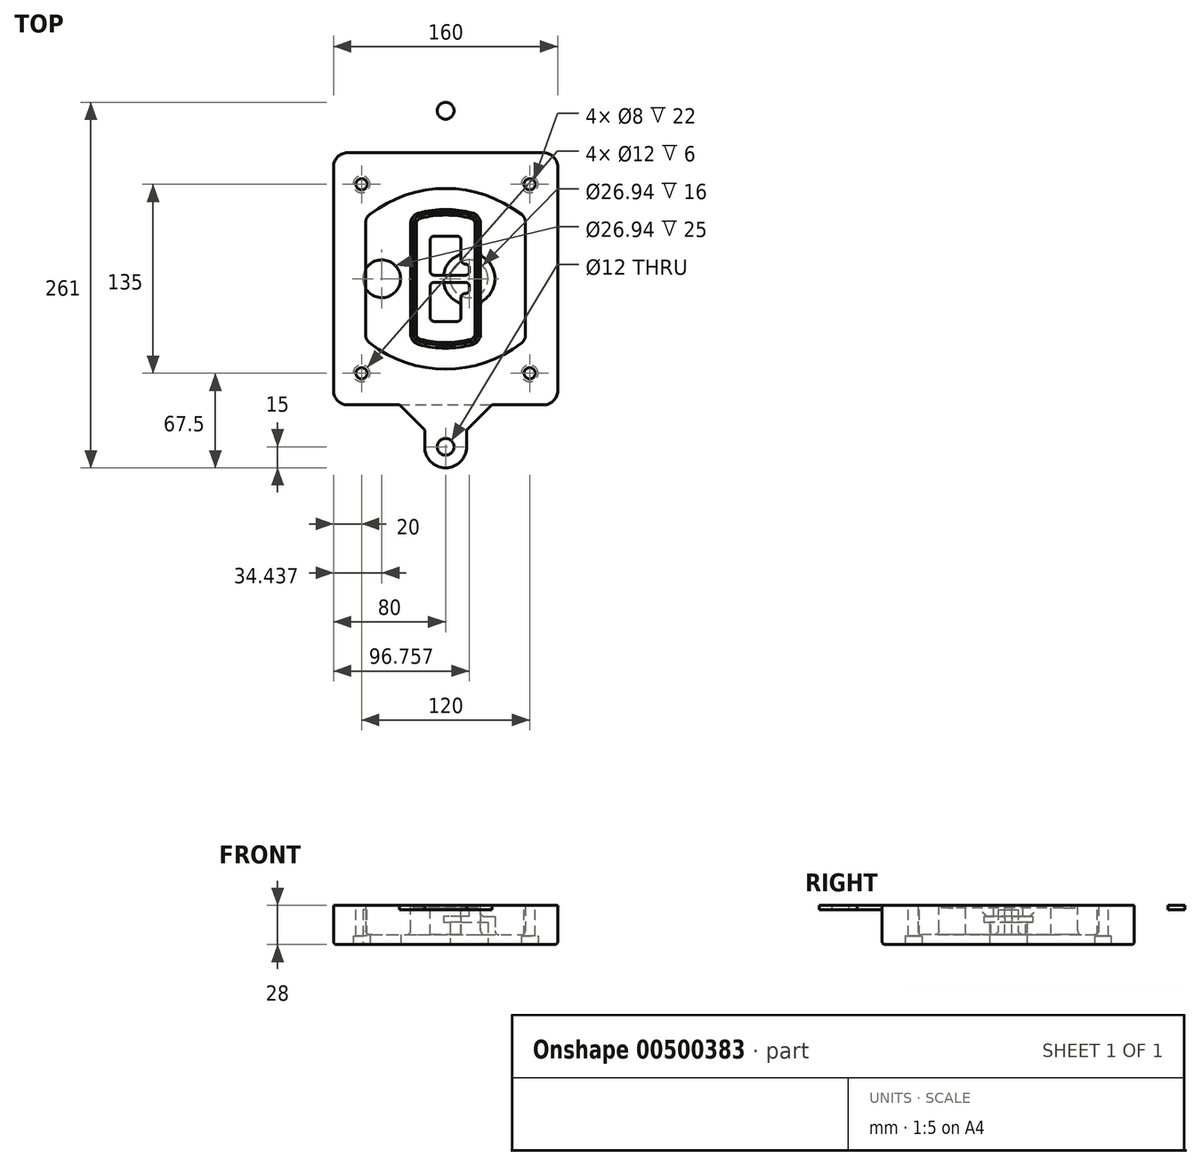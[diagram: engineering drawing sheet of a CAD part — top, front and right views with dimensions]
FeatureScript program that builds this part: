
annotation { "Feature Type Name" : "Feature", "Feature Type Description" : "" }
export const myFeature = defineFeature(function(context is Context, id is Id, definition is map)
    precondition{}
    {
        {
            var Q0;
            Q0=qCreatedBy(makeId("Top.planeOp"),FACE);
            var sketch = newSketch(context, id + "F0", { "sketchPlane" : qUnion([Q0])});
            skPoint(sketch, "E0.rect.middle", {"position": v(0, 0) * mm});
            skLineSegment(sketch, "E1.bottom", {"start": v(-70, -90) * mm, "end": v(70, -90) * mm});
            skLineSegment(sketch, "E1.top", {"start": v(-70, 90) * mm, "end": v(70, 90) * mm});
            skLineSegment(sketch, "E1.left", {"start": v(-80, -80) * mm, "end": v(-80, 80) * mm});
            skLineSegment(sketch, "E1.right", {"start": v(80, -80) * mm, "end": v(80, 80) * mm});
            skLineSegment(sketch, "E2", {"start": v(-80, 90) * mm, "end": v(80, -90) * mm, "construction": true});
            skLineSegment(sketch, "E3", {"start": v(80, 90) * mm, "end": v(-80, -90) * mm, "construction": true});
            skCircle(sketch, "E4", {"center": v(-60, 67.5) * mm, "radius": 4 * mm});
            skCircle(sketch, "E5", {"center": v(60, 67.5) * mm, "radius": 4 * mm});
            skCircle(sketch, "E6", {"center": v(60, -67.5) * mm, "radius": 4 * mm});
            skCircle(sketch, "E7", {"center": v(-60, -67.5) * mm, "radius": 4 * mm});
            skLineSegment(sketch, "E8", {"start": v(-60, 67.5) * mm, "end": v(60, 67.5) * mm, "construction": true});
            skLineSegment(sketch, "E9", {"start": v(60, 67.5) * mm, "end": v(60, -67.5) * mm, "construction": true});
            skLineSegment(sketch, "E10", {"start": v(60, -67.5) * mm, "end": v(-60, -67.5) * mm, "construction": true});
            skLineSegment(sketch, "E11", {"start": v(-60, -67.5) * mm, "end": v(-60, 67.5) * mm, "construction": true});
            skLineSegment(sketch, "E12", {"start": v(-60, 40.3) * mm, "end": v(-60, -40.3) * mm});
            skLineSegment(sketch, "E13", {"start": v(60, 40.3) * mm, "end": v(60, -40.3) * mm});
            skArc(sketch, "E14", {"start": v(56.15, 48.18) * mm, "mid": v(0, 67.5) * mm, "end": v(-56.15, 48.18) * mm});
            skArc(sketch, "E15", {"start": v(-56.15, -48.18) * mm, "mid": v(0, -67.5) * mm, "end": v(56.15, -48.18) * mm});
            skLineSegment(sketch, "E16", {"start": v(-60, 0) * mm, "end": v(60, 0) * mm, "construction": true});
            skPoint(sketch, "E17.visualSharp", {"position": v(-60, -45) * mm});
            skArc(sketch, "E17.filletArc", {"start": v(-60, -40.3) * mm, "mid": v(-58.99, -44.68) * mm, "end": v(-56.15, -48.18) * mm});
            skPoint(sketch, "E18.visualSharp", {"position": v(-60, 45) * mm});
            skArc(sketch, "E18.filletArc", {"start": v(-56.15, 48.18) * mm, "mid": v(-58.99, 44.68) * mm, "end": v(-60, 40.3) * mm});
            skPoint(sketch, "E19.visualSharp", {"position": v(60, 45) * mm});
            skArc(sketch, "E19.filletArc", {"start": v(60, 40.3) * mm, "mid": v(58.99, 44.68) * mm, "end": v(56.15, 48.18) * mm});
            skPoint(sketch, "E20.visualSharp", {"position": v(60, -45) * mm});
            skArc(sketch, "E20.filletArc", {"start": v(56.15, -48.18) * mm, "mid": v(58.99, -44.68) * mm, "end": v(60, -40.3) * mm});
            skPoint(sketch, "E21.visualSharp", {"position": v(-80, 90) * mm});
            skArc(sketch, "E21.filletArc", {"start": v(-70, 90) * mm, "mid": v(-77.07, 87.07) * mm, "end": v(-80, 80) * mm});
            skPoint(sketch, "E22.visualSharp", {"position": v(80, 90) * mm});
            skArc(sketch, "E22.filletArc", {"start": v(80, 80) * mm, "mid": v(77.07, 87.07) * mm, "end": v(70, 90) * mm});
            skPoint(sketch, "E23.visualSharp", {"position": v(80, -90) * mm});
            skArc(sketch, "E23.filletArc", {"start": v(70, -90) * mm, "mid": v(77.07, -87.07) * mm, "end": v(80, -80) * mm});
            skPoint(sketch, "E24.visualSharp", {"position": v(-80, -90) * mm});
            skArc(sketch, "E24.filletArc", {"start": v(-80, -80) * mm, "mid": v(-77.07, -87.07) * mm, "end": v(-70, -90) * mm});
            skArc(sketch, "E25.0", {"start": v(57, 40.3) * mm, "mid": v(56.3, 43.36) * mm, "end": v(54.3, 45.81) * mm});
            skLineSegment(sketch, "E25.1", {"start": v(57, 40.3) * mm, "end": v(57, -40.3) * mm});
            skArc(sketch, "E25.2", {"start": v(54.3, -45.81) * mm, "mid": v(56.3, -43.36) * mm, "end": v(57, -40.3) * mm});
            skArc(sketch, "E25.3", {"start": v(-54.3, -45.81) * mm, "mid": v(0, -64.5) * mm, "end": v(54.3, -45.81) * mm});
            skArc(sketch, "E25.4", {"start": v(-57, -40.3) * mm, "mid": v(-56.3, -43.36) * mm, "end": v(-54.3, -45.81) * mm});
            skArc(sketch, "E25.5", {"start": v(54.3, 45.81) * mm, "mid": v(0, 64.5) * mm, "end": v(-54.3, 45.81) * mm});
            skLineSegment(sketch, "E25.6", {"start": v(-57, 40.3) * mm, "end": v(-57, -40.3) * mm});
            skArc(sketch, "E25.7", {"start": v(-54.3, 45.81) * mm, "mid": v(-56.3, 43.36) * mm, "end": v(-57, 40.3) * mm});
            skArc(sketch, "E26.0", {"start": v(-58.62, 51.33) * mm, "mid": v(-62.58, 46.43) * mm, "end": v(-64, 40.3) * mm});
            skArc(sketch, "E26.1", {"start": v(58.62, 51.33) * mm, "mid": v(0, 71.5) * mm, "end": v(-58.62, 51.33) * mm});
            skArc(sketch, "E26.2", {"start": v(64, 40.3) * mm, "mid": v(62.58, 46.43) * mm, "end": v(58.62, 51.33) * mm});
            skLineSegment(sketch, "E26.3", {"start": v(64, 40.3) * mm, "end": v(64, -40.3) * mm});
            skArc(sketch, "E26.4", {"start": v(58.62, -51.33) * mm, "mid": v(62.58, -46.43) * mm, "end": v(64, -40.3) * mm});
            skLineSegment(sketch, "E26.5", {"start": v(-64, 40.3) * mm, "end": v(-64, -40.3) * mm});
            skArc(sketch, "E26.6", {"start": v(-58.62, -51.33) * mm, "mid": v(0, -71.5) * mm, "end": v(58.62, -51.33) * mm});
            skArc(sketch, "E26.7", {"start": v(-64, -40.3) * mm, "mid": v(-62.58, -46.43) * mm, "end": v(-58.62, -51.33) * mm});
            skSolve(sketch);
        }
        {
            var Q0;
            Q0=makeQuery(id+"F0.imprint","IMPRINT",FACE,{"disambiguationData":[TD([[makeQuery(id+"F0.imprint","IMPRINT",EDGE,{"derivedFrom":sQuery(id+"F0.wireOp",EDGE,"E1.bottom")}),1.0]])]});
            var Q1;
            Q1=makeQuery(id+"F0.imprint","IMPRINT",FACE,{"disambiguationData":[TD([[makeQuery(id+"F0.imprint","IMPRINT",EDGE,{"derivedFrom":sQuery(id+"F0.wireOp",EDGE,"E12")}),1.0]])]});
            var Q2;
            Q2=makeQuery(id+"F0.imprint","IMPRINT",FACE,{"disambiguationData":[TD([[makeQuery(id+"F0.imprint","IMPRINT",EDGE,{"derivedFrom":sQuery(id+"F0.wireOp",EDGE,"E25.0")}),1.0]])]});
            var Q3;
            Q3=makeQuery(id+"F0.imprint","IMPRINT",FACE,{"disambiguationData":[TD([[makeQuery(id+"F0.imprint","IMPRINT",EDGE,{"derivedFrom":sQuery(id+"F0.wireOp",EDGE,"E12")}),-1.0]])]});
            extrude(context, id + "F1", {"entities" : qUnion([Q0, Q1, Q2, Q3]), "oppositeDirection" : true, "depth" : 25 * mm});
        }
        {
            var Q0;
            Q0=makeQuery(id+"F0.imprint","IMPRINT",FACE,{"disambiguationData":[TD([[makeQuery(id+"F0.imprint","IMPRINT",EDGE,{"derivedFrom":sQuery(id+"F0.wireOp",EDGE,"E12")}),1.0]])]});
            extrude(context, id + "F2", {"entities" : qUnion([Q0]), "operationType" : NewBodyOperationType.ADD, "depth" : 3 * mm});
        }
        {
            var Q0;
            Q0=makeQuery(id+"F0.imprint","IMPRINT",FACE,{"disambiguationData":[TD([[makeQuery(id+"F0.imprint","IMPRINT",EDGE,{"derivedFrom":sQuery(id+"F0.wireOp",EDGE,"E25.0")}),1.0]])]});
            extrude(context, id + "F3", {"entities" : qUnion([Q0]), "operationType" : NewBodyOperationType.REMOVE, "oppositeDirection" : true, "depth" : 18 * mm});
        }
        {
            var Q0;
            Q0=makeQuery(id+"F2.opExtrude","CAP_FACE",FACE,{"disambiguationData":[OSD([sQuery(id+"F0.wireOp",EDGE,"E12"),sQuery(id+"F0.wireOp",EDGE,"E13"),sQuery(id+"F0.wireOp",EDGE,"E14"),sQuery(id+"F0.wireOp",EDGE,"E15"),sQuery(id+"F0.wireOp",EDGE,"E17.filletArc"),sQuery(id+"F0.wireOp",EDGE,"E18.filletArc"),sQuery(id+"F0.wireOp",EDGE,"E19.filletArc"),sQuery(id+"F0.wireOp",EDGE,"E20.filletArc"),sQuery(id+"F0.wireOp",EDGE,"E25.0"),sQuery(id+"F0.wireOp",EDGE,"E25.1"),sQuery(id+"F0.wireOp",EDGE,"E25.2"),sQuery(id+"F0.wireOp",EDGE,"E25.3"),sQuery(id+"F0.wireOp",EDGE,"E25.4"),sQuery(id+"F0.wireOp",EDGE,"E25.5"),sQuery(id+"F0.wireOp",EDGE,"E25.6"),sQuery(id+"F0.wireOp",EDGE,"E25.7")])],"isStart":false});
            var sketch = newSketch(context, id + "F4", { "sketchPlane" : qUnion([Q0])});
            skArc(sketch, "E27.0", {"start": v(-19.08, -46.97) * mm, "mid": v(0, -49.5) * mm, "end": v(19.08, -46.97) * mm});
            skArc(sketch, "E28.0", {"start": v(19.08, 46.97) * mm, "mid": v(0, 49.5) * mm, "end": v(-19.08, 46.97) * mm});
            skLineSegment(sketch, "E29", {"start": v(-25, 39.25) * mm, "end": v(-25, -39.25) * mm});
            skLineSegment(sketch, "E30", {"start": v(25, 39.25) * mm, "end": v(25, -39.25) * mm});
            skLineSegment(sketch, "E31", {"start": v(-25, 45.1) * mm, "end": v(25, 45.1) * mm, "construction": true});
            skLineSegment(sketch, "E32", {"start": v(-25, -45.1) * mm, "end": v(25, -45.1) * mm, "construction": true});
            skPoint(sketch, "E33.visualSharp", {"position": v(-25, 45.1) * mm});
            skArc(sketch, "E33.filletArc", {"start": v(-19.08, 46.97) * mm, "mid": v(-23.35, 44.11) * mm, "end": v(-25, 39.25) * mm});
            skPoint(sketch, "E34.visualSharp", {"position": v(25, 45.1) * mm});
            skArc(sketch, "E34.filletArc", {"start": v(25, 39.25) * mm, "mid": v(23.35, 44.11) * mm, "end": v(19.08, 46.97) * mm});
            skPoint(sketch, "E35.visualSharp", {"position": v(25, -45.1) * mm});
            skArc(sketch, "E35.filletArc", {"start": v(19.08, -46.97) * mm, "mid": v(23.35, -44.11) * mm, "end": v(25, -39.25) * mm});
            skPoint(sketch, "E36.visualSharp", {"position": v(-25, -45.1) * mm});
            skArc(sketch, "E36.filletArc", {"start": v(-25, -39.25) * mm, "mid": v(-23.35, -44.11) * mm, "end": v(-19.08, -46.97) * mm});
            skArc(sketch, "E37.0", {"start": v(54.3, 45.81) * mm, "mid": v(0, 64.5) * mm, "end": v(-54.3, 45.81) * mm});
            skArc(sketch, "E37.1", {"start": v(-54.3, 45.81) * mm, "mid": v(-56.3, 43.36) * mm, "end": v(-57, 40.3) * mm});
            skLineSegment(sketch, "E37.2", {"start": v(-57, 40.3) * mm, "end": v(-57, -40.3) * mm});
            skArc(sketch, "E37.3", {"start": v(-57, -40.3) * mm, "mid": v(-56.3, -43.36) * mm, "end": v(-54.3, -45.81) * mm});
            skArc(sketch, "E37.4", {"start": v(-54.3, -45.81) * mm, "mid": v(0, -64.5) * mm, "end": v(54.3, -45.81) * mm});
            skArc(sketch, "E37.5", {"start": v(54.3, -45.81) * mm, "mid": v(56.3, -43.36) * mm, "end": v(57, -40.3) * mm});
            skLineSegment(sketch, "E37.6", {"start": v(57, 40.3) * mm, "end": v(57, -40.3) * mm});
            skArc(sketch, "E37.7", {"start": v(57, 40.3) * mm, "mid": v(56.3, 43.36) * mm, "end": v(54.3, 45.81) * mm});
            skLineSegment(sketch, "E38.0", {"start": v(23, 39.25) * mm, "end": v(23, -39.25) * mm});
            skArc(sketch, "E38.1", {"start": v(18.56, -45.04) * mm, "mid": v(21.76, -42.9) * mm, "end": v(23, -39.25) * mm});
            skArc(sketch, "E38.2", {"start": v(-18.56, -45.04) * mm, "mid": v(0, -47.5) * mm, "end": v(18.56, -45.04) * mm});
            skArc(sketch, "E38.3", {"start": v(-23, -39.25) * mm, "mid": v(-21.76, -42.9) * mm, "end": v(-18.56, -45.04) * mm});
            skLineSegment(sketch, "E38.4", {"start": v(-23, 39.25) * mm, "end": v(-23, -39.25) * mm});
            skArc(sketch, "E38.5", {"start": v(23, 39.25) * mm, "mid": v(21.76, 42.9) * mm, "end": v(18.56, 45.04) * mm});
            skArc(sketch, "E38.6", {"start": v(-18.56, 45.04) * mm, "mid": v(-21.76, 42.9) * mm, "end": v(-23, 39.25) * mm});
            skArc(sketch, "E38.7", {"start": v(18.56, 45.04) * mm, "mid": v(0, 47.5) * mm, "end": v(-18.56, 45.04) * mm});
            skArc(sketch, "E39.0", {"start": v(21, 39.25) * mm, "mid": v(20.18, 41.68) * mm, "end": v(18.04, 43.1) * mm});
            skLineSegment(sketch, "E39.1", {"start": v(21, 39.25) * mm, "end": v(21, -39.25) * mm});
            skArc(sketch, "E39.2", {"start": v(18.04, -43.1) * mm, "mid": v(20.18, -41.68) * mm, "end": v(21, -39.25) * mm});
            skArc(sketch, "E39.3", {"start": v(-18.04, -43.1) * mm, "mid": v(0, -45.5) * mm, "end": v(18.04, -43.1) * mm});
            skArc(sketch, "E39.4", {"start": v(-21, -39.25) * mm, "mid": v(-20.18, -41.68) * mm, "end": v(-18.04, -43.1) * mm});
            skArc(sketch, "E39.5", {"start": v(18.04, 43.1) * mm, "mid": v(0, 45.5) * mm, "end": v(-18.04, 43.1) * mm});
            skLineSegment(sketch, "E39.6", {"start": v(-21, 39.25) * mm, "end": v(-21, -39.25) * mm});
            skArc(sketch, "E39.7", {"start": v(-18.04, 43.1) * mm, "mid": v(-20.18, 41.68) * mm, "end": v(-21, 39.25) * mm});
            skLineSegment(sketch, "E40", {"start": v(-25, 0) * mm, "end": v(25, 0) * mm, "construction": true});
            skLineSegment(sketch, "E41", {"start": v(-11, 5.5) * mm, "end": v(-11, 27.5) * mm});
            skLineSegment(sketch, "E42", {"start": v(-8, 30.5) * mm, "end": v(8, 30.5) * mm});
            skLineSegment(sketch, "E43", {"start": v(11, 27.5) * mm, "end": v(11, 13.5) * mm});
            skLineSegment(sketch, "E44", {"start": v(14, 10.5) * mm, "end": v(14, 10.5) * mm});
            skLineSegment(sketch, "E45", {"start": v(17, 7.5) * mm, "end": v(17, 5.5) * mm});
            skLineSegment(sketch, "E46", {"start": v(14, 2.5) * mm, "end": v(-8, 2.5) * mm});
            skPoint(sketch, "E47.visualSharp", {"position": v(-11, 30.5) * mm});
            skArc(sketch, "E47.filletArc", {"start": v(-8, 30.5) * mm, "mid": v(-10.12, 29.62) * mm, "end": v(-11, 27.5) * mm});
            skPoint(sketch, "E48.visualSharp", {"position": v(11, 30.5) * mm});
            skArc(sketch, "E48.filletArc", {"start": v(11, 27.5) * mm, "mid": v(10.12, 29.62) * mm, "end": v(8, 30.5) * mm});
            skPoint(sketch, "E49.visualSharp", {"position": v(11, 10.5) * mm});
            skArc(sketch, "E49.filletArc", {"start": v(11, 13.5) * mm, "mid": v(11.88, 11.38) * mm, "end": v(14, 10.5) * mm});
            skPoint(sketch, "E50.visualSharp", {"position": v(17, 10.5) * mm});
            skArc(sketch, "E50.filletArc", {"start": v(17, 7.5) * mm, "mid": v(16.12, 9.62) * mm, "end": v(14, 10.5) * mm});
            skPoint(sketch, "E51.visualSharp", {"position": v(17, 2.5) * mm});
            skArc(sketch, "E51.filletArc", {"start": v(14, 2.5) * mm, "mid": v(16.12, 3.38) * mm, "end": v(17, 5.5) * mm});
            skPoint(sketch, "E52.visualSharp", {"position": v(-11, 2.5) * mm});
            skArc(sketch, "E52.filletArc", {"start": v(-11, 5.5) * mm, "mid": v(-10.12, 3.38) * mm, "end": v(-8, 2.5) * mm});
            skLineSegment(sketch, "E53.0.MirrorCS", {"start": v(14, -2.5) * mm, "end": v(-8, -2.5) * mm});
            skArc(sketch, "E54.0.MirrorCS", {"start": v(-11, -5.5) * mm, "mid": v(-10.12, -3.38) * mm, "end": v(-8, -2.5) * mm});
            skLineSegment(sketch, "E55.0.MirrorCS", {"start": v(-11, -5.5) * mm, "end": v(-11, -27.5) * mm});
            skArc(sketch, "E56.0.MirrorCS", {"start": v(-8, -30.5) * mm, "mid": v(-10.12, -29.62) * mm, "end": v(-11, -27.5) * mm});
            skLineSegment(sketch, "E57.0.MirrorCS", {"start": v(-8, -30.5) * mm, "end": v(8, -30.5) * mm});
            skArc(sketch, "E58.0.MirrorCS", {"start": v(11, -27.5) * mm, "mid": v(10.12, -29.62) * mm, "end": v(8, -30.5) * mm});
            skLineSegment(sketch, "E59.0.MirrorCS", {"start": v(11, -27.5) * mm, "end": v(11, -13.5) * mm});
            skArc(sketch, "E60.0.MirrorCS", {"start": v(11, -13.5) * mm, "mid": v(11.88, -11.38) * mm, "end": v(14, -10.5) * mm});
            skArc(sketch, "E61.0.MirrorCS", {"start": v(17, -7.5) * mm, "mid": v(16.12, -9.62) * mm, "end": v(14, -10.5) * mm});
            skLineSegment(sketch, "E62.0.MirrorCS", {"start": v(17, -7.5) * mm, "end": v(17, -5.5) * mm});
            skArc(sketch, "E63.0.MirrorCS", {"start": v(14, -2.5) * mm, "mid": v(16.12, -3.38) * mm, "end": v(17, -5.5) * mm});
            skSolve(sketch);
        }
        {
            var Q0;
            Q0=makeQuery(id+"F4.imprint","IMPRINT",FACE,{"disambiguationData":[TD([[makeQuery(id+"F4.imprint","IMPRINT",EDGE,{"derivedFrom":sQuery(id+"F4.wireOp",EDGE,"E27.0")}),1.0]])]});
            var Q1;
            Q1=makeQuery(id+"F4.imprint","IMPRINT",FACE,{"disambiguationData":[TD([[makeQuery(id+"F4.imprint","IMPRINT",EDGE,{"derivedFrom":sQuery(id+"F4.wireOp",EDGE,"E38.0")}),-1.0]])]});
            var Q2;
            Q2=makeQuery(id+"F4.imprint","IMPRINT",FACE,{"disambiguationData":[TD([[makeQuery(id+"F4.imprint","IMPRINT",EDGE,{"derivedFrom":sQuery(id+"F4.wireOp",EDGE,"E39.0")}),1.0]])]});
            extrude(context, id + "F5", {"entities" : qUnion([Q0, Q1, Q2]), "operationType" : NewBodyOperationType.ADD, "endBound" : BoundingType.UP_TO_NEXT, "oppositeDirection" : true, "depth" : 25 * mm});
        }
        {
            var Q0;
            Q0=makeQuery(id+"F4.imprint","IMPRINT",FACE,{"disambiguationData":[TD([[makeQuery(id+"F4.imprint","IMPRINT",EDGE,{"derivedFrom":sQuery(id+"F4.wireOp",EDGE,"E38.0")}),-1.0]])]});
            extrude(context, id + "F6", {"entities" : qUnion([Q0]), "operationType" : NewBodyOperationType.REMOVE, "oppositeDirection" : true, "depth" : 2 * mm});
        }
        {
            var Q0;
            Q0=makeQuery(id+"F1.opExtrude","CAP_FACE",FACE,{"disambiguationData":[OSD([sQuery(id+"F0.wireOp",EDGE,"E1.bottom"),sQuery(id+"F0.wireOp",EDGE,"E1.top"),sQuery(id+"F0.wireOp",EDGE,"E1.left"),sQuery(id+"F0.wireOp",EDGE,"E1.right"),sQuery(id+"F0.wireOp",EDGE,"E4"),sQuery(id+"F0.wireOp",EDGE,"E5"),sQuery(id+"F0.wireOp",EDGE,"E6"),sQuery(id+"F0.wireOp",EDGE,"E7"),sQuery(id+"F0.wireOp",EDGE,"E21.filletArc"),sQuery(id+"F0.wireOp",EDGE,"E22.filletArc"),sQuery(id+"F0.wireOp",EDGE,"E23.filletArc"),sQuery(id+"F0.wireOp",EDGE,"E24.filletArc")])],"isStart":false});
            var sketch = newSketch(context, id + "F7", { "sketchPlane" : qUnion([Q0])});
            skCircle(sketch, "E64", {"center": v(16.76, 0) * mm, "radius": 13.47 * mm});
            skCircle(sketch, "E65", {"center": v(-45.56, 0) * mm, "radius": 13.47 * mm});
            skLineSegment(sketch, "E66", {"start": v(80, 0) * mm, "end": v(-80, 0) * mm});
            skCircle(sketch, "E67", {"center": v(16.76, 0) * mm, "radius": 18.47 * mm});
            skCircle(sketch, "E68", {"center": v(60, -67.5) * mm, "radius": 6 * mm});
            skCircle(sketch, "E69", {"center": v(-60, -67.5) * mm, "radius": 6 * mm});
            skCircle(sketch, "E70", {"center": v(-60, 67.5) * mm, "radius": 6 * mm});
            skCircle(sketch, "E71", {"center": v(60, 67.5) * mm, "radius": 6 * mm});
            skSolve(sketch);
        }
        {
            var Q0;
            {var subQ1=sQuery(id+"F7.wireOp",EDGE,"E66");var subQ4=sQuery(id+"F7.wireOp",EDGE,"E64");var subQ6=makeQuery(id+"F7.imprint","INTERSECT",VERTEX,{"disambiguationData":[OD(0.0)],"derivedFrom":[subQ4,subQ1]});Q0=makeQuery(id+"F7.imprint","IMPRINT",FACE,{"disambiguationData":[TD([[makeQuery(id+"F7.imprint","IMPRINT",EDGE,{"disambiguationData":[TD([[subQ6,-1.0]])],"derivedFrom":subQ4}),-1.0]])]});}
            var Q1;
            {var subQ0=sQuery(id+"F7.wireOp",EDGE,"E66");var subQ1=sQuery(id+"F7.wireOp",EDGE,"E64");var subQ3=makeQuery(id+"F7.imprint","INTERSECT",VERTEX,{"disambiguationData":[OD(0.0)],"derivedFrom":[subQ1,subQ0]});Q1=makeQuery(id+"F7.imprint","IMPRINT",FACE,{"disambiguationData":[TD([[makeQuery(id+"F7.imprint","IMPRINT",EDGE,{"disambiguationData":[TD([[subQ3,-1.0]])],"derivedFrom":subQ1}),1.0]])]});}
            var Q2;
            {var subQ0=sQuery(id+"F7.wireOp",EDGE,"E66");var subQ1=sQuery(id+"F7.wireOp",EDGE,"E64");var subQ3=makeQuery(id+"F7.imprint","INTERSECT",VERTEX,{"disambiguationData":[OD(0.0)],"derivedFrom":[subQ1,subQ0]});Q2=makeQuery(id+"F7.imprint","IMPRINT",FACE,{"disambiguationData":[TD([[makeQuery(id+"F7.imprint","IMPRINT",EDGE,{"disambiguationData":[TD([[subQ3,1.0]])],"derivedFrom":subQ1}),1.0]])]});}
            var Q3;
            {var subQ1=sQuery(id+"F7.wireOp",EDGE,"E66");var subQ4=sQuery(id+"F7.wireOp",EDGE,"E64");var subQ6=makeQuery(id+"F7.imprint","INTERSECT",VERTEX,{"disambiguationData":[OD(0.0)],"derivedFrom":[subQ4,subQ1]});Q3=makeQuery(id+"F7.imprint","IMPRINT",FACE,{"disambiguationData":[TD([[makeQuery(id+"F7.imprint","IMPRINT",EDGE,{"disambiguationData":[TD([[subQ6,1.0]])],"derivedFrom":subQ4}),-1.0]])]});}
            extrude(context, id + "F8", {"entities" : qUnion([Q0, Q1, Q2, Q3]), "operationType" : NewBodyOperationType.ADD, "oppositeDirection" : true, "depth" : 20 * mm});
        }
        {
            var Q0;
            {var subQ0=sQuery(id+"F7.wireOp",EDGE,"E66");var subQ1=sQuery(id+"F7.wireOp",EDGE,"E64");var subQ3=makeQuery(id+"F7.imprint","INTERSECT",VERTEX,{"disambiguationData":[OD(0.0)],"derivedFrom":[subQ1,subQ0]});Q0=makeQuery(id+"F7.imprint","IMPRINT",FACE,{"disambiguationData":[TD([[makeQuery(id+"F7.imprint","IMPRINT",EDGE,{"disambiguationData":[TD([[subQ3,-1.0]])],"derivedFrom":subQ1}),1.0]])]});}
            var Q1;
            {var subQ0=sQuery(id+"F7.wireOp",EDGE,"E66");var subQ1=sQuery(id+"F7.wireOp",EDGE,"E64");var subQ3=makeQuery(id+"F7.imprint","INTERSECT",VERTEX,{"disambiguationData":[OD(0.0)],"derivedFrom":[subQ1,subQ0]});Q1=makeQuery(id+"F7.imprint","IMPRINT",FACE,{"disambiguationData":[TD([[makeQuery(id+"F7.imprint","IMPRINT",EDGE,{"disambiguationData":[TD([[subQ3,1.0]])],"derivedFrom":subQ1}),1.0]])]});}
            extrude(context, id + "F9", {"entities" : qUnion([Q0, Q1]), "operationType" : NewBodyOperationType.REMOVE, "oppositeDirection" : true, "depth" : 16 * mm});
        }
        {
            var Q0;
            {var subQ0=sQuery(id+"F7.wireOp",EDGE,"E66");var subQ1=sQuery(id+"F7.wireOp",EDGE,"E65");var subQ3=makeQuery(id+"F7.imprint","INTERSECT",VERTEX,{"disambiguationData":[OD(0.0)],"derivedFrom":[subQ1,subQ0]});Q0=makeQuery(id+"F7.imprint","IMPRINT",FACE,{"disambiguationData":[TD([[makeQuery(id+"F7.imprint","IMPRINT",EDGE,{"disambiguationData":[TD([[subQ3,-1.0]])],"derivedFrom":subQ1}),1.0]])]});}
            var Q1;
            {var subQ0=sQuery(id+"F7.wireOp",EDGE,"E66");var subQ1=sQuery(id+"F7.wireOp",EDGE,"E65");var subQ3=makeQuery(id+"F7.imprint","INTERSECT",VERTEX,{"disambiguationData":[OD(0.0)],"derivedFrom":[subQ1,subQ0]});Q1=makeQuery(id+"F7.imprint","IMPRINT",FACE,{"disambiguationData":[TD([[makeQuery(id+"F7.imprint","IMPRINT",EDGE,{"disambiguationData":[TD([[subQ3,1.0]])],"derivedFrom":subQ1}),1.0]])]});}
            extrude(context, id + "F10", {"entities" : qUnion([Q0, Q1]), "operationType" : NewBodyOperationType.REMOVE, "oppositeDirection" : true, "depth" : 25 * mm});
        }
        {
            var Q0;
            Q0=makeQuery(id+"F7.imprint","IMPRINT",FACE,{"disambiguationData":[TD([[makeQuery(id+"F7.imprint","IMPRINT",EDGE,{"derivedFrom":sQuery(id+"F7.wireOp",EDGE,"E68")}),1.0]])]});
            var Q1;
            Q1=makeQuery(id+"F7.imprint","IMPRINT",FACE,{"disambiguationData":[TD([[makeQuery(id+"F7.imprint","IMPRINT",EDGE,{"derivedFrom":makeQuery(id+"F1.opExtrude","CAP_EDGE",EDGE,{"disambiguationData":[OSD([sQuery(id+"F0.wireOp",EDGE,"E5")])],"isStart":false})}),-1.0]])]});
            var Q2;
            Q2=makeQuery(id+"F7.imprint","IMPRINT",FACE,{"disambiguationData":[TD([[makeQuery(id+"F7.imprint","IMPRINT",EDGE,{"derivedFrom":sQuery(id+"F7.wireOp",EDGE,"E69")}),1.0]])]});
            var Q3;
            Q3=makeQuery(id+"F7.imprint","IMPRINT",FACE,{"disambiguationData":[TD([[makeQuery(id+"F7.imprint","IMPRINT",EDGE,{"derivedFrom":makeQuery(id+"F1.opExtrude","CAP_EDGE",EDGE,{"disambiguationData":[OSD([sQuery(id+"F0.wireOp",EDGE,"E4")])],"isStart":false})}),-1.0]])]});
            var Q4;
            Q4=makeQuery(id+"F7.imprint","IMPRINT",FACE,{"disambiguationData":[TD([[makeQuery(id+"F7.imprint","IMPRINT",EDGE,{"derivedFrom":sQuery(id+"F7.wireOp",EDGE,"E70")}),1.0]])]});
            var Q5;
            Q5=makeQuery(id+"F7.imprint","IMPRINT",FACE,{"disambiguationData":[TD([[makeQuery(id+"F7.imprint","IMPRINT",EDGE,{"derivedFrom":makeQuery(id+"F1.opExtrude","CAP_EDGE",EDGE,{"disambiguationData":[OSD([sQuery(id+"F0.wireOp",EDGE,"E7")])],"isStart":false})}),-1.0]])]});
            var Q6;
            Q6=makeQuery(id+"F7.imprint","IMPRINT",FACE,{"disambiguationData":[TD([[makeQuery(id+"F7.imprint","IMPRINT",EDGE,{"derivedFrom":sQuery(id+"F7.wireOp",EDGE,"E71")}),1.0]])]});
            var Q7;
            Q7=makeQuery(id+"F7.imprint","IMPRINT",FACE,{"disambiguationData":[TD([[makeQuery(id+"F7.imprint","IMPRINT",EDGE,{"derivedFrom":makeQuery(id+"F1.opExtrude","CAP_EDGE",EDGE,{"disambiguationData":[OSD([sQuery(id+"F0.wireOp",EDGE,"E6")])],"isStart":false})}),-1.0]])]});
            extrude(context, id + "F11", {"entities" : qUnion([Q0, Q1, Q2, Q3, Q4, Q5, Q6, Q7]), "operationType" : NewBodyOperationType.REMOVE, "oppositeDirection" : true, "depth" : 6 * mm});
        }
        {
            var Q0;
            Q0=makeQuery(id+"F9.boolean.opBoolean","COPY",FACE,{"derivedFrom":makeQuery(id+"F9.opExtrude","CAP_FACE",FACE,{"disambiguationData":[OSD([sQuery(id+"F7.wireOp",EDGE,"E64")])],"isStart":false})});
            var sketch = newSketch(context, id + "F12", { "sketchPlane" : qUnion([Q0])});
            skArc(sketch, "E72.0", {"start": v(11, 17.55) * mm, "mid": v(2.57, 11.82) * mm, "end": v(-1.54, 2.5) * mm});
            skArc(sketch, "E72.1", {"start": v(-1.54, -2.5) * mm, "mid": v(2.57, -11.82) * mm, "end": v(11, -17.55) * mm});
            skLineSegment(sketch, "E73", {"start": v(-1.54, -2.5) * mm, "end": v(14, -2.5) * mm});
            skLineSegment(sketch, "E74.0", {"start": v(14, 2.5) * mm, "end": v(-1.54, 2.5) * mm});
            skArc(sketch, "E74.1", {"start": v(14, 2.5) * mm, "mid": v(16.12, 3.38) * mm, "end": v(17, 5.5) * mm});
            skLineSegment(sketch, "E74.2", {"start": v(17, 7.5) * mm, "end": v(17, 5.5) * mm});
            skArc(sketch, "E74.3", {"start": v(17, 7.5) * mm, "mid": v(16.12, 9.62) * mm, "end": v(14, 10.5) * mm});
            skArc(sketch, "E74.4", {"start": v(11, 13.5) * mm, "mid": v(11.88, 11.38) * mm, "end": v(14, 10.5) * mm});
            skLineSegment(sketch, "E74.5", {"start": v(11, 17.55) * mm, "end": v(11, 13.5) * mm});
            skLineSegment(sketch, "E74.7", {"start": v(14, -2.5) * mm, "end": v(-1.54, -2.5) * mm});
            skArc(sketch, "E74.8", {"start": v(14, -2.5) * mm, "mid": v(16.12, -3.38) * mm, "end": v(17, -5.5) * mm});
            skLineSegment(sketch, "E74.9", {"start": v(17, -7.5) * mm, "end": v(17, -5.5) * mm});
            skArc(sketch, "E74.10", {"start": v(17, -7.5) * mm, "mid": v(16.12, -9.62) * mm, "end": v(14, -10.5) * mm});
            skArc(sketch, "E74.11", {"start": v(11, -13.5) * mm, "mid": v(11.88, -11.38) * mm, "end": v(14, -10.5) * mm});
            skLineSegment(sketch, "E74.12", {"start": v(11, -17.55) * mm, "end": v(11, -13.5) * mm});
            skPoint(sketch, "E75.orphan", {"position": v(11, -27.5) * mm});
            skPoint(sketch, "E76.orphan", {"position": v(-8, -2.5) * mm});
            skPoint(sketch, "E77.orphan", {"position": v(-8, 2.5) * mm});
            skPoint(sketch, "E78.orphan", {"position": v(11, 27.5) * mm});
            skSolve(sketch);
        }
        {
            var Q0;
            {var subQ7=sQuery(id+"F12.wireOp",EDGE,"E72.0");var subQ14=sQuery(id+"F12.wireOp",EDGE,"E72.1");var subQ16=sQuery(id+"F12.wireOp",EDGE,"E74.1");var subQ18=sQuery(id+"F12.wireOp",EDGE,"E74.8");Q0=qUnion([makeQuery(id+"F12.imprint","IMPRINT",FACE,{"disambiguationData":[TD([[makeQuery(id+"F12.imprint","IMPRINT",EDGE,{"derivedFrom":subQ7}),1.0]])]}),makeQuery(id+"F12.imprint","IMPRINT",FACE,{"disambiguationData":[TD([[makeQuery(id+"F12.imprint","IMPRINT",EDGE,{"derivedFrom":subQ14}),1.0]])]}),makeQuery(id+"F12.imprint","IMPRINT",FACE,{"disambiguationData":[TD([[makeQuery(id+"F12.imprint","IMPRINT",EDGE,{"derivedFrom":subQ16}),1.0]])]}),makeQuery(id+"F12.imprint","IMPRINT",FACE,{"disambiguationData":[TD([[makeQuery(id+"F12.imprint","IMPRINT",EDGE,{"derivedFrom":subQ18}),-1.0]])]})]);}
            var Q1;
            Q1=makeQuery(id+"F5.boolean.opBoolean","SPLIT",FACE,{"disambiguationData":[TD([makeQuery(id+"F5.opExtrude","SWEPT_FACE",FACE,{"disambiguationData":[OSD([sQuery(id+"F4.wireOp",EDGE,"E41")])]})])],"derivedFrom":makeQuery(id+"F3.boolean.opBoolean","COPY",FACE,{"derivedFrom":makeQuery(id+"F3.opExtrude","CAP_FACE",FACE,{"disambiguationData":[OSD([sQuery(id+"F0.wireOp",EDGE,"E25.0"),sQuery(id+"F0.wireOp",EDGE,"E25.1"),sQuery(id+"F0.wireOp",EDGE,"E25.2"),sQuery(id+"F0.wireOp",EDGE,"E25.3"),sQuery(id+"F0.wireOp",EDGE,"E25.4"),sQuery(id+"F0.wireOp",EDGE,"E25.5"),sQuery(id+"F0.wireOp",EDGE,"E25.6"),sQuery(id+"F0.wireOp",EDGE,"E25.7")])],"isStart":false})})});
            extrude(context, id + "F13", {"entities" : qUnion([Q0]), "operationType" : NewBodyOperationType.REMOVE, "endBound" : BoundingType.UP_TO_SURFACE, "endBoundEntityFace" : qUnion([Q1]), "depth" : 25 * mm});
        }
        {
            var Q0;
            Q0=makeQuery(id+"F3.boolean.opBoolean","COPY",EDGE,{"derivedFrom":makeQuery(id+"F3.opExtrude","CAP_EDGE",EDGE,{"disambiguationData":[OSD([sQuery(id+"F0.wireOp",EDGE,"E25.6")])],"isStart":false})});
            var Q1;
            Q1=makeQuery(id+"F8.boolean.opBoolean","INTERSECT",EDGE,{"derivedFrom":[makeQuery(id+"F5.opExtrude","SWEPT_FACE",FACE,{"disambiguationData":[OSD([sQuery(id+"F4.wireOp",EDGE,"E30")])]}),makeQuery(id+"F8.opExtrude","CAP_FACE",FACE,{"disambiguationData":[OSD([sQuery(id+"F7.wireOp",EDGE,"E67")])],"isStart":false})]});
            var Q2;
            Q2=makeQuery(id+"F8.boolean.opBoolean","INTERSECT",EDGE,{"disambiguationData":[OD(1.0)],"derivedFrom":[makeQuery(id+"F5.opExtrude","SWEPT_FACE",FACE,{"disambiguationData":[OSD([sQuery(id+"F4.wireOp",EDGE,"E30")])]}),makeQuery(id+"F8.opExtrude","SWEPT_FACE",FACE,{"disambiguationData":[OSD([sQuery(id+"F7.wireOp",EDGE,"E67")])]})]});
            var Q3;
            {var subQ0=sQuery(id+"F4.wireOp",EDGE,"E30");Q3=makeQuery(id+"F8.boolean.opBoolean","SPLIT",EDGE,{"disambiguationData":[TD([makeQuery(id+"F5.opExtrude","SWEPT_FACE",FACE,{"disambiguationData":[OSD([sQuery(id+"F4.wireOp",EDGE,"E35.filletArc")])]})])],"derivedFrom":makeQuery(id+"F5.opExtrude","CAP_EDGE",EDGE,{"disambiguationData":[OSD([subQ0])],"isStart":false})});}
            var Q4;
            {var subQ0=sQuery(id+"F0.wireOp",EDGE,"E25.7");var subQ1=sQuery(id+"F0.wireOp",EDGE,"E25.1");var subQ2=sQuery(id+"F0.wireOp",EDGE,"E25.6");var subQ3=sQuery(id+"F0.wireOp",EDGE,"E25.5");var subQ4=sQuery(id+"F0.wireOp",EDGE,"E25.4");var subQ5=sQuery(id+"F0.wireOp",EDGE,"E25.0");var subQ6=sQuery(id+"F0.wireOp",EDGE,"E25.2");var subQ7=sQuery(id+"F0.wireOp",EDGE,"E25.3");Q4=makeQuery(id+"F8.boolean.opBoolean","INTERSECT",EDGE,{"derivedFrom":[makeQuery(id+"F5.boolean.opBoolean","SPLIT",FACE,{"disambiguationData":[TD([makeQuery(id+"F2.opExtrude","SWEPT_FACE",FACE,{"disambiguationData":[OSD([subQ5])]})])],"derivedFrom":makeQuery(id+"F3.boolean.opBoolean","COPY",FACE,{"derivedFrom":makeQuery(id+"F3.opExtrude","CAP_FACE",FACE,{"disambiguationData":[OSD([subQ5,subQ1,subQ6,subQ7,subQ4,subQ3,subQ2,subQ0])],"isStart":false})})}),makeQuery(id+"F8.opExtrude","SWEPT_FACE",FACE,{"disambiguationData":[OSD([sQuery(id+"F7.wireOp",EDGE,"E67")])]})]});}
            var Q5;
            Q5=makeQuery(id+"F8.boolean.opBoolean","INTERSECT",EDGE,{"disambiguationData":[OD(0.0)],"derivedFrom":[makeQuery(id+"F5.opExtrude","SWEPT_FACE",FACE,{"disambiguationData":[OSD([sQuery(id+"F4.wireOp",EDGE,"E30")])]}),makeQuery(id+"F8.opExtrude","SWEPT_FACE",FACE,{"disambiguationData":[OSD([sQuery(id+"F7.wireOp",EDGE,"E67")])]})]});
            fillet(context, id + "F14", {"entities" : qUnion([Q0, Q1, Q2, Q3, Q4, Q5]), "radius" : 3 * mm, "tangentPropagation" : true, "allowEdgeOverflow" : false});
        }
        {
            var Q0;
            Q0=makeQuery(id+"F1.opExtrude","CAP_EDGE",EDGE,{"disambiguationData":[OSD([sQuery(id+"F0.wireOp",EDGE,"E1.bottom")])],"isStart":false});
            fillet(context, id + "F15", {"entities" : qUnion([Q0]), "radius" : 2 * mm, "tangentPropagation" : true, "allowEdgeOverflow" : false});
        }
        {
            var Q0;
            {var subQ0=sQuery(id+"F0.wireOp",EDGE,"E21.filletArc");var subQ1=sQuery(id+"F0.wireOp",EDGE,"E7");var subQ2=sQuery(id+"F0.wireOp",EDGE,"E6");var subQ3=sQuery(id+"F0.wireOp",EDGE,"E5");var subQ4=sQuery(id+"F0.wireOp",EDGE,"E4");var subQ5=sQuery(id+"F0.wireOp",EDGE,"E22.filletArc");var subQ6=sQuery(id+"F0.wireOp",EDGE,"E1.bottom");var subQ7=sQuery(id+"F0.wireOp",EDGE,"E1.right");var subQ8=sQuery(id+"F0.wireOp",EDGE,"E1.top");var subQ9=sQuery(id+"F0.wireOp",EDGE,"E1.left");var subQ10=sQuery(id+"F0.wireOp",EDGE,"E23.filletArc");var subQ11=sQuery(id+"F0.wireOp",EDGE,"E24.filletArc");Q0=makeQuery(id+"F2.boolean.opBoolean","SPLIT",FACE,{"disambiguationData":[TD([makeQuery(id+"F1.opExtrude","SWEPT_FACE",FACE,{"disambiguationData":[OSD([subQ6])]})])],"derivedFrom":makeQuery(id+"F1.opExtrude","CAP_FACE",FACE,{"disambiguationData":[OSD([subQ6,subQ8,subQ9,subQ7,subQ4,subQ3,subQ2,subQ1,subQ0,subQ5,subQ10,subQ11])],"isStart":true})});}
            var sketch = newSketch(context, id + "F16", { "sketchPlane" : qUnion([Q0])});
            skCircle(sketch, "E79", {"center": v(0, 41.16) * mm, "radius": 0.18 * mm});
            skLineSegment(sketch, "E80", {"start": v(0, 90) * mm, "end": v(0, 120) * mm, "construction": true});
            skCircle(sketch, "E81", {"center": v(0, 120) * mm, "radius": 6 * mm});
            skLineSegment(sketch, "E82", {"start": v(-33, 90) * mm, "end": v(-15, 108) * mm});
            skLineSegment(sketch, "E83", {"start": v(33, 90) * mm, "end": v(15, 108) * mm});
            skLineSegment(sketch, "E84", {"start": v(-15, 108) * mm, "end": v(-15, 120) * mm});
            skLineSegment(sketch, "E85", {"start": v(15, 108) * mm, "end": v(15, 120) * mm});
            skArc(sketch, "E86", {"start": v(15, 120) * mm, "mid": v(0, 135) * mm, "end": v(-15, 120) * mm});
            skLineSegment(sketch, "E87", {"start": v(-80, 0) * mm, "end": v(80, 0) * mm, "construction": true});
            skArc(sketch, "E88.MirrorCS", {"start": v(15, -120) * mm, "mid": v(0, -135) * mm, "end": v(-15, -120) * mm});
            skLineSegment(sketch, "E89.MirrorCS", {"start": v(15, -108) * mm, "end": v(15, -120) * mm});
            skLineSegment(sketch, "E90.MirrorCS", {"start": v(33, -90) * mm, "end": v(15, -108) * mm});
            skLineSegment(sketch, "E91.MirrorCS", {"start": v(-33, -90) * mm, "end": v(-15, -108) * mm});
            skLineSegment(sketch, "E92.MirrorCS", {"start": v(-15, -108) * mm, "end": v(-15, -120) * mm});
            skCircle(sketch, "E93.MirrorC", {"center": v(0, -120) * mm, "radius": 6 * mm});
            skLineSegment(sketch, "E94.MirrorCS", {"start": v(0, -90) * mm, "end": v(0, -120) * mm, "construction": true});
            skSolve(sketch);
        }
        {
            var Q0;
            Q0=makeQuery(id+"F16.imprint","IMPRINT",FACE,{"disambiguationData":[TD([[makeQuery(id+"F16.imprint","IMPRINT",EDGE,{"derivedFrom":sQuery(id+"F16.wireOp",EDGE,"E89.MirrorCS")}),-1.0]])]});
            var Q1;
            Q1=makeQuery(id+"F16.imprint","IMPRINT",FACE,{"disambiguationData":[TD([[makeQuery(id+"F16.imprint","IMPRINT",EDGE,{"derivedFrom":makeQuery(id+"F1.opExtrude","CAP_EDGE",EDGE,{"disambiguationData":[OSD([sQuery(id+"F0.wireOp",EDGE,"E1.left")])],"isStart":true})}),-1.0]])]});
            var Q2;
            Q2=makeQuery(id+"F16.imprint","IMPRINT",FACE,{"disambiguationData":[TD([[makeQuery(id+"F16.imprint","IMPRINT",EDGE,{"derivedFrom":sQuery(id+"F16.wireOp",EDGE,"E81")}),1.0]])]});
            var Q3;
            Q3=makeQuery(id+"F2.opExtrude","CAP_FACE",FACE,{"disambiguationData":[OSD([sQuery(id+"F0.wireOp",EDGE,"E12"),sQuery(id+"F0.wireOp",EDGE,"E13"),sQuery(id+"F0.wireOp",EDGE,"E14"),sQuery(id+"F0.wireOp",EDGE,"E15"),sQuery(id+"F0.wireOp",EDGE,"E17.filletArc"),sQuery(id+"F0.wireOp",EDGE,"E18.filletArc"),sQuery(id+"F0.wireOp",EDGE,"E19.filletArc"),sQuery(id+"F0.wireOp",EDGE,"E20.filletArc"),sQuery(id+"F0.wireOp",EDGE,"E25.0"),sQuery(id+"F0.wireOp",EDGE,"E25.1"),sQuery(id+"F0.wireOp",EDGE,"E25.2"),sQuery(id+"F0.wireOp",EDGE,"E25.3"),sQuery(id+"F0.wireOp",EDGE,"E25.4"),sQuery(id+"F0.wireOp",EDGE,"E25.5"),sQuery(id+"F0.wireOp",EDGE,"E25.6"),sQuery(id+"F0.wireOp",EDGE,"E25.7")])],"isStart":false});
            extrude(context, id + "F17", {"entities" : qUnion([Q0, Q1, Q2]), "operationType" : NewBodyOperationType.ADD, "endBound" : BoundingType.UP_TO_SURFACE, "endBoundEntityFace" : qUnion([Q3]), "depth" : 25 * mm});
        }
    });
